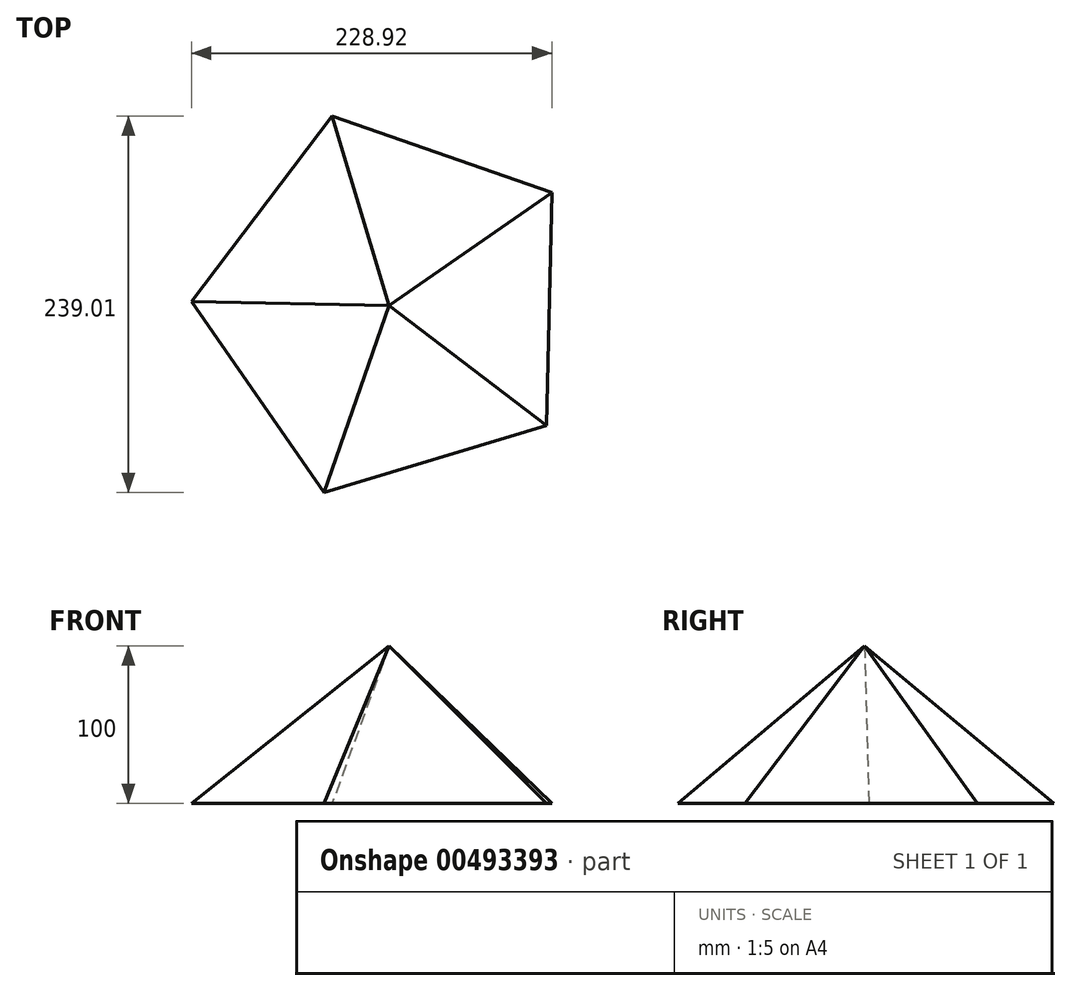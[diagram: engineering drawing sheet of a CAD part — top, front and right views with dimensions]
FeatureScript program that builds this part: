
annotation { "Feature Type Name" : "Feature", "Feature Type Description" : "" }
export const myFeature = defineFeature(function(context is Context, id is Id, definition is map)
    precondition{}
    {
        {
            var Q0;
            Q0=qCreatedBy(makeId("Top.planeOp"),FACE);
            var sketch = newSketch(context, id + "F0", { "sketchPlane" : qUnion([Q0])});
            skCircle(sketch, "E0.cCircle", {"center": v(0, 0) * mm, "radius": 125.69 * mm, "construction": true});
            skLineSegment(sketch, "E0.0", {"start": v(-125.66, 2.73) * mm, "end": v(-36.24, 120.35) * mm});
            skLineSegment(sketch, "E0.1", {"start": v(-36.24, 120.35) * mm, "end": v(103.26, 71.65) * mm});
            skLineSegment(sketch, "E0.2", {"start": v(103.26, 71.65) * mm, "end": v(100.06, -76.06) * mm});
            skLineSegment(sketch, "E0.3", {"start": v(100.06, -76.06) * mm, "end": v(-41.42, -118.66) * mm});
            skLineSegment(sketch, "E0.4", {"start": v(-41.42, -118.66) * mm, "end": v(-125.66, 2.73) * mm});
            skSolve(sketch);
        }
        {
            var Q0;
            Q0=qCreatedBy(makeId("Top.planeOp"),FACE);
            cPlane(context, id + "F1", {"entities" : qUnion([Q0]), "cplaneType" : CPlaneType.OFFSET, "offset" : 100 * mm, "width" : 150 * mm, "height" : 150 * mm});
        }
        {
            var Q0;
            Q0=qCreatedBy(id+"F1.planeOp",FACE);
            var sketch = newSketch(context, id + "F2", { "sketchPlane" : qUnion([Q0])});
            skPoint(sketch, "E1", {"position": v(0, 0) * mm});
            skSolve(sketch);
        }
        {
            var Q0;
            Q0=sQuery(id+"F2.wireOp",VERTEX,"E1");
            var Q1;
            Q1=makeQuery(id+"F0.imprint","IMPRINT",FACE,{"disambiguationData":[TD([[makeQuery(id+"F0.imprint","IMPRINT",EDGE,{"derivedFrom":sQuery(id+"F0.wireOp",EDGE,"E0.0")}),-1.0]])]});
            loft(context, id + "F3", {"sheetProfilesArray" : [{ "sheetProfileEntities" : qUnion([Q0]) }, { "sheetProfileEntities" : qUnion([Q1]) }]});
        }
    });
